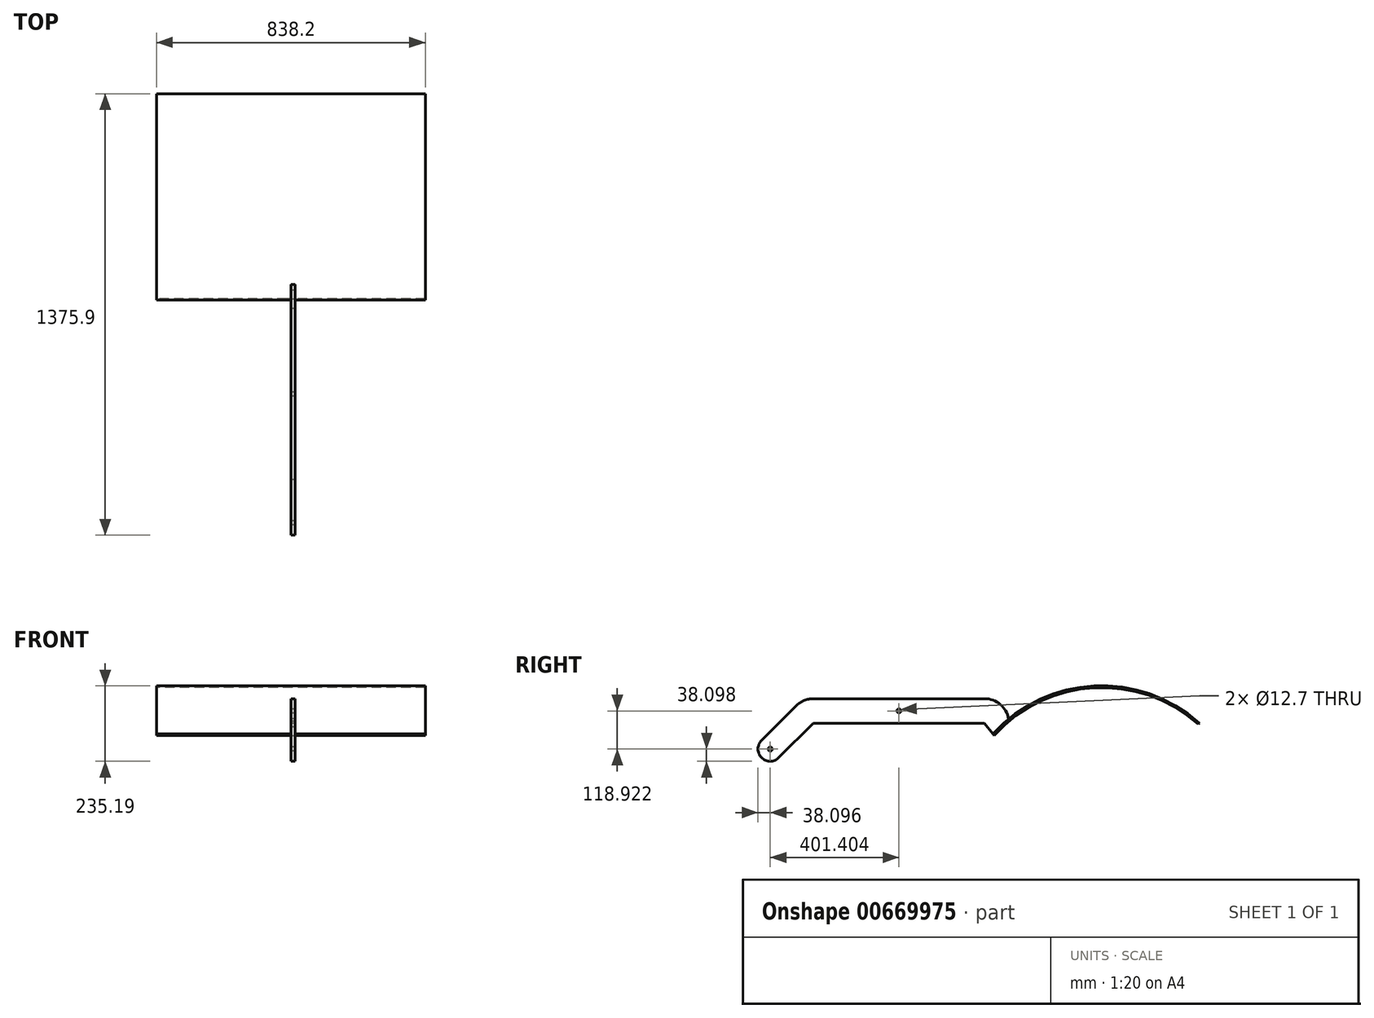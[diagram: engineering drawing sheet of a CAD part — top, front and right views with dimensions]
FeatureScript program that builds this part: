
annotation { "Feature Type Name" : "Feature", "Feature Type Description" : "" }
export const myFeature = defineFeature(function(context is Context, id is Id, definition is map)
    precondition{}
    {
        {
            var Q0;
            Q0=qCreatedBy(makeId("Right.planeOp"),FACE);
            var sketch = newSketch(context, id + "F0", { "sketchPlane" : qUnion([Q0])});
            skCircle(sketch, "E0", {"center": v(0, 0) * mm, "radius": 6.35 * mm});
            skLineSegment(sketch, "E1.bottom", {"start": v(-266.7, 38.1) * mm, "end": v(266.7, 38.1) * mm});
            skLineSegment(sketch, "E1.top", {"start": v(-266.7, -38.1) * mm, "end": v(266.7, -38.1) * mm});
            skLineSegment(sketch, "E1.left", {"start": v(-266.7, 38.1) * mm, "end": v(-266.7, -38.1) * mm});
            skLineSegment(sketch, "E1.right", {"start": v(266.7, 38.1) * mm, "end": v(266.7, -38.1) * mm});
            skArc(sketch, "E2", {"start": v(266.7, 38.1) * mm, "mid": v(320.58, 15.78) * mm, "end": v(342.9, -38.1) * mm});
            skLineSegment(sketch, "E3.bottom", {"start": v(266.7, -38.1) * mm, "end": v(342.9, -38.1) * mm});
            skLineSegment(sketch, "E3.top", {"start": v(266.7, -88.9) * mm, "end": v(342.9, -88.9) * mm});
            skLineSegment(sketch, "E3.left", {"start": v(266.7, -38.1) * mm, "end": v(266.7, -88.9) * mm});
            skLineSegment(sketch, "E3.right", {"start": v(342.9, -38.1) * mm, "end": v(342.9, -88.9) * mm});
            skArc(sketch, "E4", {"start": v(-266.7, 38.1) * mm, "mid": v(-295.86, 32.3) * mm, "end": v(-320.58, 15.78) * mm});
            skLineSegment(sketch, "E5", {"start": v(-320.58, 15.78) * mm, "end": v(-266.7, -38.1) * mm});
            skLineSegment(sketch, "E6", {"start": v(-320.58, 15.78) * mm, "end": v(-428.34, -91.98) * mm});
            skLineSegment(sketch, "E7", {"start": v(-428.34, -91.98) * mm, "end": v(-374.46, -145.86) * mm});
            skLineSegment(sketch, "E8", {"start": v(-374.46, -145.86) * mm, "end": v(-266.7, -38.1) * mm});
            skArc(sketch, "E9", {"start": v(-374.46, -145.86) * mm, "mid": v(-428.34, -145.86) * mm, "end": v(-428.34, -91.98) * mm});
            skCircle(sketch, "E10", {"center": v(-401.4, -118.92) * mm, "radius": 6.35 * mm});
            skSolve(sketch);
        }
        {
            var Q0;
            Q0 = qSketchRegion(id + "F0", true);
            extrude(context, id + "F1", {"entities" : qUnion([Q0]), "depth" : 12.7 * mm, "offsetDistance" : 25.4 * mm});
        }
        {
            var Q0;
            Q0=makeQuery(id+"F1.opExtrude","CAP_FACE",FACE,{"disambiguationData":[OSD([sQuery(id+"F0.wireOp",EDGE,"E0"),sQuery(id+"F0.wireOp",EDGE,"E1.bottom"),sQuery(id+"F0.wireOp",EDGE,"E1.top"),sQuery(id+"F0.wireOp",EDGE,"ywCUUmKd-35c3-DdLO-dEnt-KZ58f2ZC2MwI"),sQuery(id+"F0.wireOp",EDGE,"E2"),sQuery(id+"F0.wireOp",EDGE,"E3.top"),sQuery(id+"F0.wireOp",EDGE,"E3.left"),sQuery(id+"F0.wireOp",EDGE,"E3.right"),sQuery(id+"F0.wireOp",EDGE,"KRHbE7VX-L1Lb-qWxd-P7e2-YFSgQER6LuLe")])],"isStart":false});
            var sketch = newSketch(context, id + "F2", { "sketchPlane" : qUnion([Q0])});
            skArc(sketch, "E11", {"start": v(936.4, -38.1) * mm, "mid": v(607.84, 77.56) * mm, "end": v(293.01, -71.47) * mm});
            skArc(sketch, "E12", {"start": v(932.98, -41.86) * mm, "mid": v(607.9, 71.9) * mm, "end": v(297, -76.3) * mm});
            skLineSegment(sketch, "E13", {"start": v(293.01, -71.47) * mm, "end": v(297, -76.3) * mm});
            skLineSegment(sketch, "E14", {"start": v(936.4, -38.1) * mm, "end": v(932.98, -41.86) * mm});
            skSolve(sketch);
        }
        {
            var Q0;
            Q0 = qSketchRegion(id + "F2", true);
            extrude(context, id + "F3", {"entities" : qUnion([Q0]), "operationType" : NewBodyOperationType.ADD, "depth" : 406.4 * mm, "offsetDistance" : 25.4 * mm, "hasSecondDirection" : true, "secondDirectionOppositeDirection" : true, "secondDirectionDepth" : 431.8 * mm});
        }
        {
            var Q0;
            Q0=makeQuery(id+"F1.opExtrude","CAP_FACE",FACE,{"disambiguationData":[OSD([sQuery(id+"F0.wireOp",EDGE,"E0"),sQuery(id+"F0.wireOp",EDGE,"E1.bottom"),sQuery(id+"F0.wireOp",EDGE,"E1.top"),sQuery(id+"F0.wireOp",EDGE,"E2"),sQuery(id+"F0.wireOp",EDGE,"E3.top"),sQuery(id+"F0.wireOp",EDGE,"E3.left"),sQuery(id+"F0.wireOp",EDGE,"E3.right"),sQuery(id+"F0.wireOp",EDGE,"E4"),sQuery(id+"F0.wireOp",EDGE,"E6"),sQuery(id+"F0.wireOp",EDGE,"E8"),sQuery(id+"F0.wireOp",EDGE,"E9"),sQuery(id+"F0.wireOp",EDGE,"E10")])],"isStart":false});
            var sketch = newSketch(context, id + "F4", { "sketchPlane" : qUnion([Q0])});
            skLineSegment(sketch, "E15", {"start": v(342.9, -88.9) * mm, "end": v(266.7, -88.9) * mm});
            skLineSegment(sketch, "E16", {"start": v(266.7, -88.9) * mm, "end": v(266.7, -38.1) * mm});
            skLineSegment(sketch, "E17", {"start": v(266.7, -38.1) * mm, "end": v(297, -76.3) * mm});
            skLineSegment(sketch, "E18", {"start": v(297, -76.3) * mm, "end": v(324.45, -48.46) * mm});
            skLineSegment(sketch, "E19", {"start": v(324.45, -48.46) * mm, "end": v(342.69, -32.4) * mm});
            skLineSegment(sketch, "E20", {"start": v(342.69, -32.4) * mm, "end": v(347.13, -30.68) * mm});
            skLineSegment(sketch, "E21", {"start": v(347.13, -30.68) * mm, "end": v(347.13, -88.77) * mm});
            skLineSegment(sketch, "E22", {"start": v(347.13, -88.77) * mm, "end": v(342.9, -88.9) * mm});
            skSolve(sketch);
        }
        {
            var Q0;
            Q0 = qSketchRegion(id + "F4", true);
            extrude(context, id + "F5", {"entities" : qUnion([Q0]), "operationType" : NewBodyOperationType.REMOVE, "oppositeDirection" : true, "depth" : 25.4 * mm, "offsetDistance" : 25.4 * mm});
        }
    });
